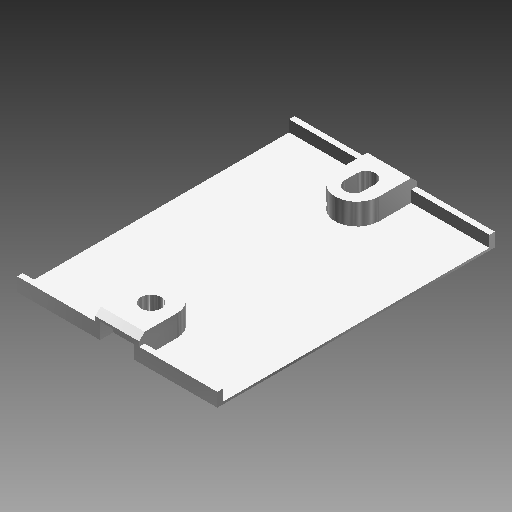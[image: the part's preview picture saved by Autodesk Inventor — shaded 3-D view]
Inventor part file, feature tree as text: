
AUTODESK INVENTOR PART (.ipt)
format: ipt  version: 2019 (Build 230136000, 136)  size: 200,192 bytes
history: native  units: in
note: dims shown in document units (in); Inventor stores cm internally (conversion verified against a paired STEP export)
features: extrude x6, sketch x6, chamfer x1
ambient origin geometry x8: Origin, YZ Plane, XZ Plane, XY Plane, X Axis, Y Axis, Z Axis, Center Point
bodies: Solid1 (feature_tree)
feature tree (13):
  extrude  "Extrusion1"  Depth=1.769in
  extrude  "Extrusion2"  Depth=0.049in
  extrude  "Extrusion3"  Depth=2.355in
  extrude  "Extrusion4"  Depth=0.1in TaperAngle=0.0deg
  chamfer  "Chamfer1"  Distance=0.194in
  extrude  "Extrusion5"  Depth=0.388in
  extrude  "Extrusion6"  Depth=0.142in
  sketch  "Sketch1"  dims[d0=2.453in d1=1.769in]
  sketch  "Sketch2"  dims[d2=0.021in d3=0.0in d4=0.049in]
  sketch  "Sketch3"  dims[d5=0.049in d6=2.355in]
  sketch  "Sketch4"  dims[d7=0.0in d8=0.1in d9=0.0in]
  sketch  "Sketch5"  dims[d10=0.478in]
  sketch  "Sketch6"  dims[d11=0.388in d12=0.194in d13=0.388in d14=0.478in d15=0.194in d16=0.194in d17=0.19in d18=0.0in d19=0.09in d20=0.0in d21=0.049in d22=0.125in d23=45.0deg d24=0.303in d25=0.117in d26=0.117in d27=0.142in d28=0.0in d29=0.165in d30=0.274in d31=0.169in d32=0.0825in d33=0.0825in d34=0.0825in d35=0.3in d36=0.142in d37=0.0in d38=0.178in]
